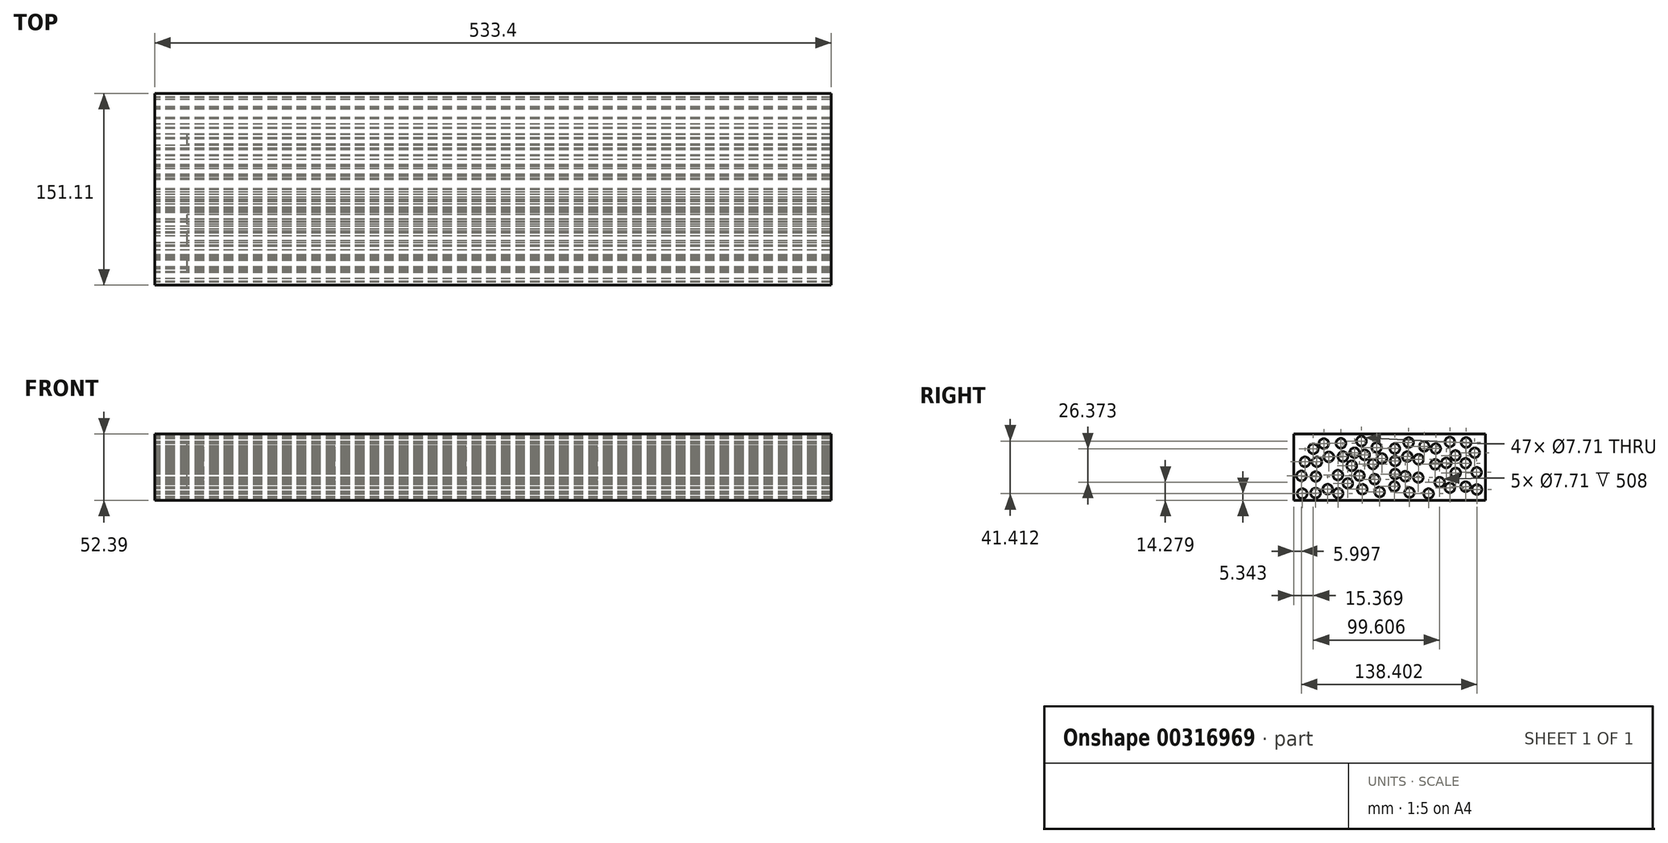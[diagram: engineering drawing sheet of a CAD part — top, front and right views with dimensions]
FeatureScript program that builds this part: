
annotation { "Feature Type Name" : "Feature", "Feature Type Description" : "" }
export const myFeature = defineFeature(function(context is Context, id is Id, definition is map)
    precondition{}
    {
        {
            var Q0;
            Q0=qCreatedBy(makeId("Right.planeOp"),FACE);
            var sketch = newSketch(context, id + "F0", { "sketchPlane" : qUnion([Q0])});
            skLineSegment(sketch, "E0.bottom", {"start": v(-76.38, 61.34) * mm, "end": v(74.73, 61.34) * mm});
            skLineSegment(sketch, "E0.top", {"start": v(-76.38, 8.95) * mm, "end": v(74.73, 8.95) * mm});
            skLineSegment(sketch, "E0.left", {"start": v(-76.38, 61.34) * mm, "end": v(-76.38, 8.95) * mm});
            skLineSegment(sketch, "E0.right", {"start": v(74.73, 61.34) * mm, "end": v(74.73, 8.95) * mm});
            skLineSegment(sketch, "E1.bottom", {"start": v(-76.7, -8.37) * mm, "end": v(74.73, -8.37) * mm});
            skLineSegment(sketch, "E1.top", {"start": v(-76.7, -58.29) * mm, "end": v(74.73, -58.29) * mm});
            skLineSegment(sketch, "E1.left", {"start": v(-76.7, -8.37) * mm, "end": v(-76.7, -58.29) * mm});
            skLineSegment(sketch, "E1.right", {"start": v(74.73, -8.37) * mm, "end": v(74.73, -58.29) * mm});
            skCircle(sketch, "E2", {"center": v(-69.95, 55.7) * mm, "radius": 3.86 * mm});
            skCircle(sketch, "E3", {"center": v(-67.55, 39.36) * mm, "radius": 3.86 * mm});
            skCircle(sketch, "E4", {"center": v(-48.8, 43.28) * mm, "radius": 3.86 * mm});
            skCircle(sketch, "E5", {"center": v(-59.05, 27.8) * mm, "radius": 3.86 * mm});
            skCircle(sketch, "E6", {"center": v(-49.68, 17.78) * mm, "radius": 3.86 * mm});
            skCircle(sketch, "E7", {"center": v(-30.72, 36.3) * mm, "radius": 3.86 * mm});
            skCircle(sketch, "E8", {"center": v(-22.43, 17.78) * mm, "radius": 3.86 * mm});
            skCircle(sketch, "E9", {"center": v(-41.61, 28.9) * mm, "radius": 3.86 * mm});
            skCircle(sketch, "E10", {"center": v(-28.54, 46.55) * mm, "radius": 3.86 * mm});
            skCircle(sketch, "E11", {"center": v(-13.93, 37.61) * mm, "radius": 3.86 * mm});
            skCircle(sketch, "E12", {"center": v(-12.62, 25.63) * mm, "radius": 3.86 * mm});
            skCircle(sketch, "E13", {"center": v(21.81, 26.93) * mm, "radius": 3.86 * mm});
            skCircle(sketch, "E14", {"center": v(13.1, 43.5) * mm, "radius": 3.86 * mm});
            skCircle(sketch, "E15", {"center": v(-11.1, 50.7) * mm, "radius": 3.86 * mm});
            skCircle(sketch, "E16", {"center": v(3.5, 29.77) * mm, "radius": 3.86 * mm});
            skCircle(sketch, "E17", {"center": v(2.85, 19.96) * mm, "radius": 3.86 * mm});
            skCircle(sketch, "E18", {"center": v(-8.7, 15.6) * mm, "radius": 3.86 * mm});
            skCircle(sketch, "E19", {"center": v(-6.96, 41.97) * mm, "radius": 3.86 * mm});
            skCircle(sketch, "E20", {"center": v(3.29, 49.82) * mm, "radius": 3.86 * mm});
            skCircle(sketch, "E21", {"center": v(26.39, 51.56) * mm, "radius": 3.86 * mm});
            skCircle(sketch, "E22", {"center": v(35.1, 37.4) * mm, "radius": 3.86 * mm});
            skCircle(sketch, "E23", {"center": v(38.6, 23.23) * mm, "radius": 3.86 * mm});
            skCircle(sketch, "E24", {"center": v(59.08, 19.74) * mm, "radius": 3.86 * mm});
            skCircle(sketch, "E25", {"center": v(59.08, 38.27) * mm, "radius": 3.86 * mm});
            skCircle(sketch, "E26", {"center": v(51.02, 44.37) * mm, "radius": 3.86 * mm});
            skCircle(sketch, "E27", {"center": v(51.24, 30.64) * mm, "radius": 3.86 * mm});
            skCircle(sketch, "E28", {"center": v(46.66, 18.87) * mm, "radius": 3.86 * mm});
            skCircle(sketch, "E29", {"center": v(29.88, 14.3) * mm, "radius": 3.86 * mm});
            skCircle(sketch, "E30", {"center": v(14.84, 15.16) * mm, "radius": 3.86 * mm});
            skCircle(sketch, "E31", {"center": v(11.57, 28.02) * mm, "radius": 3.86 * mm});
            skCircle(sketch, "E32", {"center": v(3.5, 40.01) * mm, "radius": 3.86 * mm});
            skCircle(sketch, "E33", {"center": v(22.03, 41.32) * mm, "radius": 3.86 * mm});
            skCircle(sketch, "E34", {"center": v(35.54, 49.82) * mm, "radius": 3.86 * mm});
            skCircle(sketch, "E35", {"center": v(59.52, 54.61) * mm, "radius": 3.86 * mm});
            skCircle(sketch, "E36", {"center": v(66.28, 46.55) * mm, "radius": 3.86 * mm});
            skCircle(sketch, "E37", {"center": v(67.8, 31.08) * mm, "radius": 3.86 * mm});
            skCircle(sketch, "E38", {"center": v(68.02, 17.56) * mm, "radius": 3.86 * mm});
            skCircle(sketch, "E39", {"center": v(-52.73, 53.74) * mm, "radius": 3.86 * mm});
            skCircle(sketch, "E40", {"center": v(-61.01, 49.6) * mm, "radius": 3.86 * mm});
            skCircle(sketch, "E41", {"center": v(-58.18, 39.36) * mm, "radius": 3.86 * mm});
            skCircle(sketch, "E42", {"center": v(-39.22, 53.96) * mm, "radius": 3.86 * mm});
            skCircle(sketch, "E43", {"center": v(-37.69, 43.5) * mm, "radius": 3.86 * mm});
            skCircle(sketch, "E44", {"center": v(-33.77, 22.36) * mm, "radius": 3.86 * mm});
            skCircle(sketch, "E45", {"center": v(-24.61, 28.46) * mm, "radius": 3.86 * mm});
            skCircle(sketch, "E46", {"center": v(-41.4, 14.51) * mm, "radius": 3.86 * mm});
            skCircle(sketch, "E47", {"center": v(-59.27, 14.73) * mm, "radius": 3.86 * mm});
            skCircle(sketch, "E48", {"center": v(-69.73, 14.3) * mm, "radius": 3.86 * mm});
            skCircle(sketch, "E49", {"center": v(-70.38, 28.24) * mm, "radius": 3.86 * mm});
            skCircle(sketch, "E50", {"center": v(-23.09, 55.7) * mm, "radius": 3.86 * mm});
            skCircle(sketch, "E51", {"center": v(-20.47, 44.8) * mm, "radius": 3.86 * mm});
            skCircle(sketch, "E52", {"center": v(14.18, 54.61) * mm, "radius": 3.86 * mm});
            skCircle(sketch, "E53", {"center": v(46.66, 55.05) * mm, "radius": 3.86 * mm});
            skCircle(sketch, "E54", {"center": v(43.83, 38.49) * mm, "radius": 3.86 * mm});
            skCircle(sketch, "E55", {"center": v(-49.68, -38.89) * mm, "radius": 3.86 * mm});
            skCircle(sketch, "E56", {"center": v(-28.97, -30.39) * mm, "radius": 3.86 * mm});
            skCircle(sketch, "E57", {"center": v(-15.46, -36.27) * mm, "radius": 3.86 * mm});
            skCircle(sketch, "E58", {"center": v(24.2, -36.27) * mm, "radius": 3.86 * mm});
            skCircle(sketch, "E59", {"center": v(-14.37, -47.82) * mm, "radius": 3.86 * mm});
            skCircle(sketch, "E60", {"center": v(4.81, -24.07) * mm, "radius": 3.86 * mm});
            skCircle(sketch, "E61", {"center": v(8.3, -34.75) * mm, "radius": 3.86 * mm});
            skCircle(sketch, "E62", {"center": v(-66.9, -20.36) * mm, "radius": 3.86 * mm});
            skCircle(sketch, "E63", {"center": v(-66.24, -40.63) * mm, "radius": 3.86 * mm});
            skCircle(sketch, "E64", {"center": v(-49.68, -26.68) * mm, "radius": 3.86 * mm});
            skCircle(sketch, "E65", {"center": v(-17.86, -17.53) * mm, "radius": 3.86 * mm});
            skCircle(sketch, "E66", {"center": v(13.31, -49.13) * mm, "radius": 3.86 * mm});
            skCircle(sketch, "E67", {"center": v(59.95, -45.64) * mm, "radius": 3.86 * mm});
            skCircle(sketch, "E68", {"center": v(61.04, -33.88) * mm, "radius": 3.86 * mm});
            skCircle(sketch, "E69", {"center": v(65.62, -19.27) * mm, "radius": 3.86 * mm});
            skCircle(sketch, "E70", {"center": v(41.86, -19.5) * mm, "radius": 3.86 * mm});
            skCircle(sketch, "E71", {"center": v(29.22, -20.8) * mm, "radius": 3.86 * mm});
            skCircle(sketch, "E72", {"center": v(40.12, -42.81) * mm, "radius": 3.86 * mm});
            skCircle(sketch, "E73", {"center": v(-44.01, -46.95) * mm, "radius": 3.86 * mm});
            skCircle(sketch, "E74", {"center": v(-37.25, -18.18) * mm, "radius": 3.86 * mm});
            skCircle(sketch, "E75", {"center": v(-49.68, -16.44) * mm, "radius": 3.86 * mm});
            skCircle(sketch, "E76", {"center": v(-29.84, -45.86) * mm, "radius": 3.86 * mm});
            skCircle(sketch, "E77", {"center": v(-58.61, -48.48) * mm, "radius": 3.86 * mm});
            skCircle(sketch, "E78", {"center": v(-66.02, -51.75) * mm, "radius": 3.86 * mm});
            skCircle(sketch, "E79", {"center": v(-6.09, -25.16) * mm, "radius": 3.86 * mm});
            skCircle(sketch, "E80", {"center": v(16.15, -15.78) * mm, "radius": 3.86 * mm});
            skCircle(sketch, "E81", {"center": v(29.44, -50) * mm, "radius": 3.86 * mm});
            skCircle(sketch, "E82", {"center": v(-5.43, -45.2) * mm, "radius": 3.86 * mm});
            skCircle(sketch, "E83", {"center": v(-64.5, -28.64) * mm, "radius": 3.86 * mm});
            skCircle(sketch, "E84", {"center": v(-38.78, -30.17) * mm, "radius": 3.86 * mm});
            skCircle(sketch, "E85", {"center": v(-6.3, -14.26) * mm, "radius": 3.86 * mm});
            skCircle(sketch, "E86", {"center": v(40.12, -30.39) * mm, "radius": 3.86 * mm});
            skCircle(sketch, "E87", {"center": v(17.89, -26.68) * mm, "radius": 3.86 * mm});
            skCircle(sketch, "E88", {"center": v(52.33, -13.6) * mm, "radius": 3.86 * mm});
            skCircle(sketch, "E89", {"center": v(52.76, -26.25) * mm, "radius": 3.86 * mm});
            skCircle(sketch, "E90", {"center": v(49.93, -36.5) * mm, "radius": 3.86 * mm});
            skCircle(sketch, "E91", {"center": v(49.93, -47.6) * mm, "radius": 3.86 * mm});
            skCircle(sketch, "E92", {"center": v(4.6, -42.16) * mm, "radius": 3.86 * mm});
            skCircle(sketch, "E93", {"center": v(-3.9, -34.75) * mm, "radius": 3.86 * mm});
            skCircle(sketch, "E94", {"center": v(-20.9, -26.46) * mm, "radius": 3.86 * mm});
            skCircle(sketch, "E95", {"center": v(-28.75, -17.1) * mm, "radius": 3.86 * mm});
            skCircle(sketch, "E96", {"center": v(-59.05, -14.04) * mm, "radius": 3.86 * mm});
            skCircle(sketch, "E97", {"center": v(66.93, -52.18) * mm, "radius": 3.86 * mm});
            skCircle(sketch, "E98", {"center": v(39.68, -51.31) * mm, "radius": 3.86 * mm});
            skCircle(sketch, "E99", {"center": v(30.1, -30.6) * mm, "radius": 3.86 * mm});
            skCircle(sketch, "E100", {"center": v(-37.25, -51.97) * mm, "radius": 3.86 * mm});
            skCircle(sketch, "E101", {"center": v(-38.56, -39.98) * mm, "radius": 3.86 * mm});
            skCircle(sketch, "E102", {"center": v(2.2, -53.27) * mm, "radius": 3.86 * mm});
            skSolve(sketch);
        }
        {
            var Q0;
            Q0=sQuery(id+"F0.wireOp",EDGE,"E3");
            extrude(context, id + "F1", {"bodyType" : ToolBodyType.SURFACE, "surfaceEntities" : qUnion([Q0]), "depth" : 508 * mm});
        }
        {
            var Q0;
            Q0=makeQuery(id+"F0.imprint","IMPRINT",FACE,{"disambiguationData":[TD([[makeQuery(id+"F0.imprint","IMPRINT",EDGE,{"derivedFrom":sQuery(id+"F0.wireOp",EDGE,"E2")}),1.0]])]});
            var Q1;
            Q1=makeQuery(id+"F0.imprint","IMPRINT",FACE,{"disambiguationData":[TD([[makeQuery(id+"F0.imprint","IMPRINT",EDGE,{"derivedFrom":sQuery(id+"F0.wireOp",EDGE,"E0.bottom")}),-1.0]])]});
            extrude(context, id + "F2", {"entities" : qUnion([Q0, Q1]), "depth" : 508 * mm});
        }
        {
            var Q0;
            Q0=makeQuery(id+"F0.imprint","IMPRINT",FACE,{"disambiguationData":[TD([[makeQuery(id+"F0.imprint","IMPRINT",EDGE,{"derivedFrom":sQuery(id+"F0.wireOp",EDGE,"E40")}),1.0]])]});
            extrude(context, id + "F3", {"entities" : qUnion([Q0]), "operationType" : NewBodyOperationType.ADD, "depth" : 25.4 * mm});
        }
        {
            var Q0;
            Q0=makeQuery(id+"F2.opExtrude","CAP_FACE",FACE,{"disambiguationData":[OSD([sQuery(id+"F0.wireOp",EDGE,"E0.bottom"),sQuery(id+"F0.wireOp",EDGE,"E0.top"),sQuery(id+"F0.wireOp",EDGE,"E0.left"),sQuery(id+"F0.wireOp",EDGE,"E0.right"),sQuery(id+"F0.wireOp",EDGE,"E3"),sQuery(id+"F0.wireOp",EDGE,"E4"),sQuery(id+"F0.wireOp",EDGE,"E5"),sQuery(id+"F0.wireOp",EDGE,"E6"),sQuery(id+"F0.wireOp",EDGE,"E7"),sQuery(id+"F0.wireOp",EDGE,"E8"),sQuery(id+"F0.wireOp",EDGE,"E9"),sQuery(id+"F0.wireOp",EDGE,"E10"),sQuery(id+"F0.wireOp",EDGE,"E11"),sQuery(id+"F0.wireOp",EDGE,"E12"),sQuery(id+"F0.wireOp",EDGE,"E13"),sQuery(id+"F0.wireOp",EDGE,"E14"),sQuery(id+"F0.wireOp",EDGE,"E15"),sQuery(id+"F0.wireOp",EDGE,"E16"),sQuery(id+"F0.wireOp",EDGE,"E17"),sQuery(id+"F0.wireOp",EDGE,"E18"),sQuery(id+"F0.wireOp",EDGE,"E19"),sQuery(id+"F0.wireOp",EDGE,"E20"),sQuery(id+"F0.wireOp",EDGE,"E21"),sQuery(id+"F0.wireOp",EDGE,"E22"),sQuery(id+"F0.wireOp",EDGE,"E23"),sQuery(id+"F0.wireOp",EDGE,"E24"),sQuery(id+"F0.wireOp",EDGE,"E25"),sQuery(id+"F0.wireOp",EDGE,"E26"),sQuery(id+"F0.wireOp",EDGE,"E27"),sQuery(id+"F0.wireOp",EDGE,"E28"),sQuery(id+"F0.wireOp",EDGE,"E29"),sQuery(id+"F0.wireOp",EDGE,"E30"),sQuery(id+"F0.wireOp",EDGE,"E31"),sQuery(id+"F0.wireOp",EDGE,"E32"),sQuery(id+"F0.wireOp",EDGE,"E33"),sQuery(id+"F0.wireOp",EDGE,"E34"),sQuery(id+"F0.wireOp",EDGE,"E35"),sQuery(id+"F0.wireOp",EDGE,"E36"),sQuery(id+"F0.wireOp",EDGE,"E37"),sQuery(id+"F0.wireOp",EDGE,"E38"),sQuery(id+"F0.wireOp",EDGE,"E39"),sQuery(id+"F0.wireOp",EDGE,"E40"),sQuery(id+"F0.wireOp",EDGE,"E41"),sQuery(id+"F0.wireOp",EDGE,"E42"),sQuery(id+"F0.wireOp",EDGE,"E43"),sQuery(id+"F0.wireOp",EDGE,"E44"),sQuery(id+"F0.wireOp",EDGE,"E45"),sQuery(id+"F0.wireOp",EDGE,"E46"),sQuery(id+"F0.wireOp",EDGE,"E47"),sQuery(id+"F0.wireOp",EDGE,"E48"),sQuery(id+"F0.wireOp",EDGE,"E49"),sQuery(id+"F0.wireOp",EDGE,"E50"),sQuery(id+"F0.wireOp",EDGE,"E51"),sQuery(id+"F0.wireOp",EDGE,"E52"),sQuery(id+"F0.wireOp",EDGE,"E53"),sQuery(id+"F0.wireOp",EDGE,"E54")])],"isStart":false});
            var Q1;
            Q1=makeQuery(id+"F0.imprint","IMPRINT",FACE,{"disambiguationData":[TD([[makeQuery(id+"F0.imprint","IMPRINT",EDGE,{"derivedFrom":sQuery(id+"F0.wireOp",EDGE,"E9")}),1.0]])]});
            var Q2;
            Q2=makeQuery(id+"F0.imprint","IMPRINT",FACE,{"disambiguationData":[TD([[makeQuery(id+"F0.imprint","IMPRINT",EDGE,{"derivedFrom":sQuery(id+"F0.wireOp",EDGE,"E43")}),1.0]])]});
            var Q3;
            Q3=makeQuery(id+"F0.imprint","IMPRINT",FACE,{"disambiguationData":[TD([[makeQuery(id+"F0.imprint","IMPRINT",EDGE,{"derivedFrom":sQuery(id+"F0.wireOp",EDGE,"E45")}),1.0]])]});
            var Q4;
            Q4=makeQuery(id+"F0.imprint","IMPRINT",FACE,{"disambiguationData":[TD([[makeQuery(id+"F0.imprint","IMPRINT",EDGE,{"derivedFrom":sQuery(id+"F0.wireOp",EDGE,"E23")}),1.0]])]});
            extrude(context, id + "F4", {"entities" : qUnion([Q0, Q1, Q2, Q3, Q4]), "operationType" : NewBodyOperationType.ADD, "depth" : 25.4 * mm});
        }
    });
